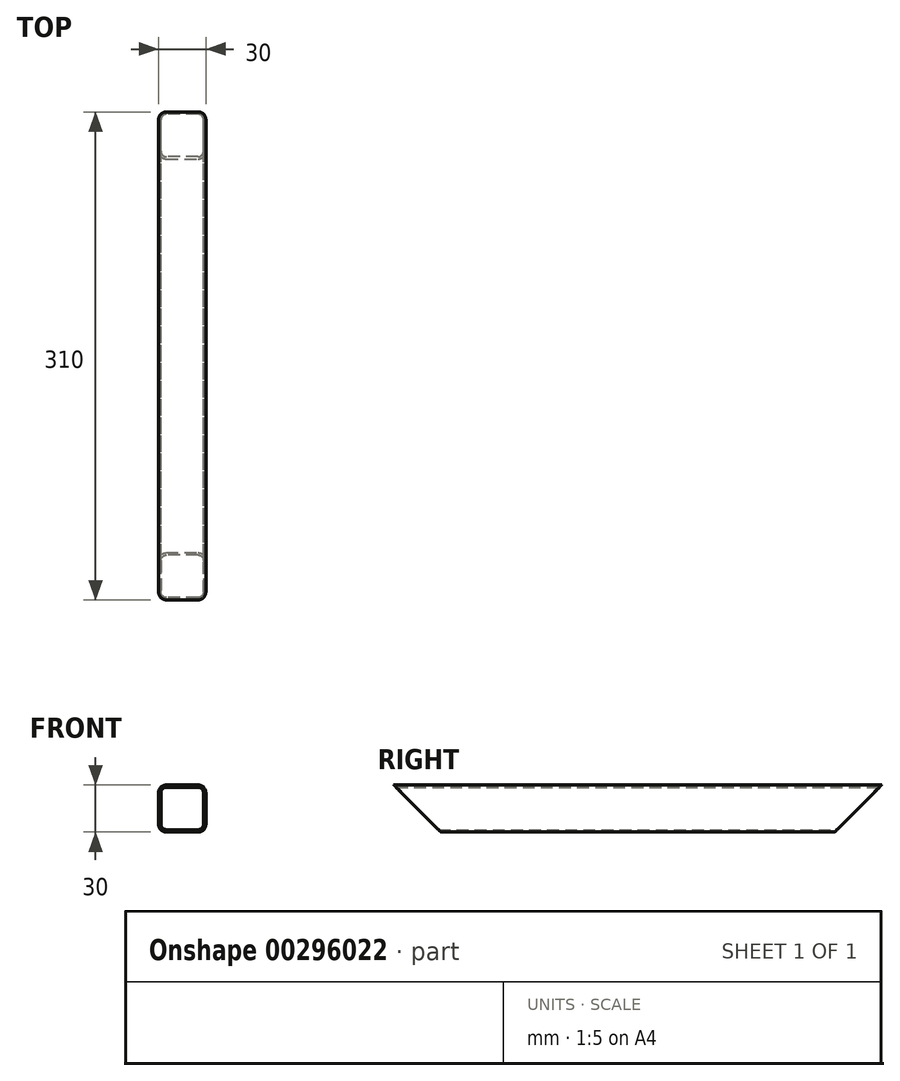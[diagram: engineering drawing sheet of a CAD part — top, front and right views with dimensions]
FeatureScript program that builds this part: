
annotation { "Feature Type Name" : "Feature", "Feature Type Description" : "" }
export const myFeature = defineFeature(function(context is Context, id is Id, definition is map)
    precondition{}
    {
        {
            var Q0;
            Q0=qCreatedBy(makeId("Front.planeOp"),FACE);
            var sketch = newSketch(context, id + "F0", { "sketchPlane" : qUnion([Q0])});
            skLineSegment(sketch, "E0.bottom", {"start": v(10, -15) * mm, "end": v(-10, -15) * mm});
            skLineSegment(sketch, "E0.top", {"start": v(10, 15) * mm, "end": v(-10, 15) * mm});
            skLineSegment(sketch, "E0.left", {"start": v(15, -10) * mm, "end": v(15, 10) * mm});
            skLineSegment(sketch, "E0.right", {"start": v(-15, -10) * mm, "end": v(-15, 10) * mm});
            skPoint(sketch, "E0.middle", {"position": v(0, 0) * mm});
            skPoint(sketch, "E1.visualSharp", {"position": v(-15, 15) * mm});
            skArc(sketch, "E1.filletArc", {"start": v(-10, 15) * mm, "mid": v(-13.54, 13.54) * mm, "end": v(-15, 10) * mm});
            skPoint(sketch, "E2.visualSharp", {"position": v(15, 15) * mm});
            skArc(sketch, "E2.filletArc", {"start": v(15, 10) * mm, "mid": v(13.54, 13.54) * mm, "end": v(10, 15) * mm});
            skPoint(sketch, "E3.visualSharp", {"position": v(15, -15) * mm});
            skArc(sketch, "E3.filletArc", {"start": v(10, -15) * mm, "mid": v(13.54, -13.54) * mm, "end": v(15, -10) * mm});
            skPoint(sketch, "E4.visualSharp", {"position": v(-15, -15) * mm});
            skArc(sketch, "E4.filletArc", {"start": v(-15, -10) * mm, "mid": v(-13.54, -13.54) * mm, "end": v(-10, -15) * mm});
            skLineSegment(sketch, "E5.0", {"start": v(-13.5, -10) * mm, "end": v(-13.5, 10) * mm});
            skLineSegment(sketch, "E5.1", {"start": v(10, -13.5) * mm, "end": v(-10, -13.5) * mm});
            skLineSegment(sketch, "E5.2", {"start": v(13.5, -10) * mm, "end": v(13.5, 10) * mm});
            skLineSegment(sketch, "E5.3", {"start": v(10, 13.5) * mm, "end": v(-10, 13.5) * mm});
            skPoint(sketch, "E6.visualSharp", {"position": v(-13.5, 13.5) * mm});
            skArc(sketch, "E6.filletArc", {"start": v(-10, 13.5) * mm, "mid": v(-12.47, 12.47) * mm, "end": v(-13.5, 10) * mm});
            skPoint(sketch, "E7.visualSharp", {"position": v(13.5, 13.5) * mm});
            skArc(sketch, "E7.filletArc", {"start": v(13.5, 10) * mm, "mid": v(12.47, 12.47) * mm, "end": v(10, 13.5) * mm});
            skPoint(sketch, "E8.visualSharp", {"position": v(13.5, -13.5) * mm});
            skArc(sketch, "E8.filletArc", {"start": v(10, -13.5) * mm, "mid": v(12.47, -12.47) * mm, "end": v(13.5, -10) * mm});
            skPoint(sketch, "E9.visualSharp", {"position": v(-13.5, -13.5) * mm});
            skArc(sketch, "E9.filletArc", {"start": v(-13.5, -10) * mm, "mid": v(-12.47, -12.47) * mm, "end": v(-10, -13.5) * mm});
            skSolve(sketch);
        }
        {
            var Q0;
            Q0=qSketchRegion(id+"F0",true);
            extrude(context, id + "F1", {"entities" : qUnion([Q0]), "depth" : 310 * mm});
        }
        {
            var Q0;
            Q0=makeQuery(id+"F1.opExtrude","SWEPT_FACE",FACE,{"disambiguationData":[OSD([sQuery(id+"F0.wireOp",EDGE,"E0.left")])]});
            var sketch = newSketch(context, id + "F2", { "sketchPlane" : qUnion([Q0])});
            skLineSegment(sketch, "E10", {"start": v(0, 15) * mm, "end": v(-30, -15) * mm});
            skLineSegment(sketch, "E11", {"start": v(-30, -15) * mm, "end": v(0, -15) * mm});
            skLineSegment(sketch, "E12", {"start": v(0, -15) * mm, "end": v(0, 15) * mm});
            skLineSegment(sketch, "E13", {"start": v(-155, 19.77) * mm, "end": v(-155, -19.95) * mm, "construction": true});
            skLineSegment(sketch, "E14.MirrorCS", {"start": v(-310, -15) * mm, "end": v(-310, 15) * mm});
            skLineSegment(sketch, "E15.MirrorCS", {"start": v(-310, 15) * mm, "end": v(-280, -15) * mm});
            skLineSegment(sketch, "E16.MirrorCS", {"start": v(-280, -15) * mm, "end": v(-310, -15) * mm});
            skSolve(sketch);
        }
        {
            var Q0;
            Q0=qSketchRegion(id+"F2",true);
            extrude(context, id + "F3", {"entities" : qUnion([Q0]), "operationType" : NewBodyOperationType.REMOVE, "endBound" : BoundingType.THROUGH_ALL, "oppositeDirection" : true, "depth" : 25 * mm});
        }
    });
